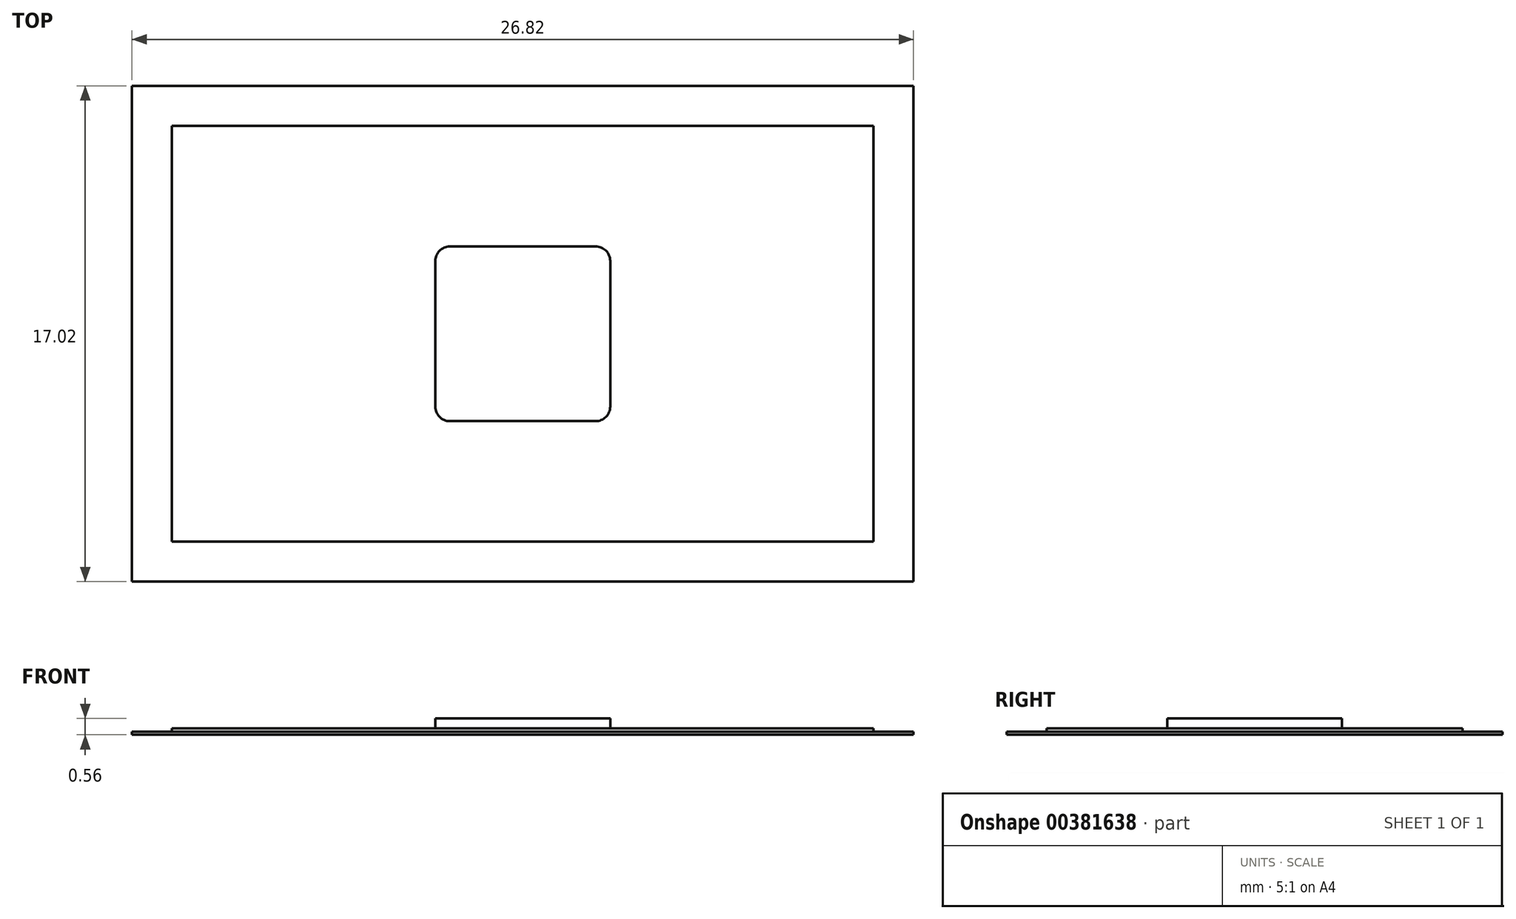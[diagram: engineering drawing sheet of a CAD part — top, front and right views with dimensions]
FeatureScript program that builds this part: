
annotation { "Feature Type Name" : "Feature", "Feature Type Description" : "" }
export const myFeature = defineFeature(function(context is Context, id is Id, definition is map)
    precondition{}
    {
        {
            var Q0;
            Q0=qCreatedBy(makeId("Top.planeOp"),FACE);
            var sketch = newSketch(context, id + "F0", { "sketchPlane" : qUnion([Q0])});
            skLineSegment(sketch, "E0.bottom", {"start": v(-12.29, 6.19) * mm, "end": v(14.53, 6.19) * mm});
            skLineSegment(sketch, "E0.top", {"start": v(-12.29, -10.83) * mm, "end": v(14.53, -10.83) * mm});
            skLineSegment(sketch, "E0.left", {"start": v(-12.29, 6.19) * mm, "end": v(-12.29, -10.83) * mm});
            skLineSegment(sketch, "E0.right", {"start": v(14.53, 6.19) * mm, "end": v(14.53, -10.83) * mm});
            skSolve(sketch);
        }
        {
            var Q0;
            Q0=makeQuery(id+"F0.imprint","IMPRINT",FACE,{"disambiguationData":[TD([[makeQuery(id+"F0.imprint","IMPRINT",EDGE,{"derivedFrom":sQuery(id+"F0.wireOp",EDGE,"E0.bottom")}),-1.0]])]});
            extrude(context, id + "F1", {"entities" : qUnion([Q0]), "depth" : 0.1 * mm});
        }
        {
            var Q0;
            Q0=makeQuery(id+"F1.opExtrude","CAP_FACE",FACE,{"disambiguationData":[OSD([sQuery(id+"F0.wireOp",EDGE,"E0.bottom"),sQuery(id+"F0.wireOp",EDGE,"E0.top"),sQuery(id+"F0.wireOp",EDGE,"E0.left"),sQuery(id+"F0.wireOp",EDGE,"E0.right")])],"isStart":false});
            var sketch = newSketch(context, id + "F2", { "sketchPlane" : qUnion([Q0])});
            skLineSegment(sketch, "E1.bottom", {"start": v(-10.92, 4.82) * mm, "end": v(13.16, 4.82) * mm});
            skLineSegment(sketch, "E1.top", {"start": v(-10.92, -9.46) * mm, "end": v(13.16, -9.46) * mm});
            skLineSegment(sketch, "E1.left", {"start": v(-10.92, 4.82) * mm, "end": v(-10.92, -9.46) * mm});
            skLineSegment(sketch, "E1.right", {"start": v(13.16, 4.82) * mm, "end": v(13.16, -9.46) * mm});
            skSolve(sketch);
        }
        {
            var Q0;
            Q0=makeQuery(id+"F2.imprint","IMPRINT",FACE,{"disambiguationData":[TD([[makeQuery(id+"F2.imprint","IMPRINT",EDGE,{"derivedFrom":sQuery(id+"F2.wireOp",EDGE,"E1.bottom")}),-1.0]])]});
            extrude(context, id + "F3", {"entities" : qUnion([Q0]), "operationType" : NewBodyOperationType.ADD, "depth" : 0.1 * mm});
        }
        {
            var Q0;
            Q0=makeQuery(id+"F3.opExtrude","CAP_FACE",FACE,{"disambiguationData":[OSD([sQuery(id+"F2.wireOp",EDGE,"E1.bottom"),sQuery(id+"F2.wireOp",EDGE,"E1.top"),sQuery(id+"F2.wireOp",EDGE,"E1.left"),sQuery(id+"F2.wireOp",EDGE,"E1.right")])],"isStart":false});
            var sketch = newSketch(context, id + "F4", { "sketchPlane" : qUnion([Q0])});
            skLineSegment(sketch, "E2.bottom", {"start": v(-1.38, 0.68) * mm, "end": v(3.62, 0.68) * mm});
            skLineSegment(sketch, "E2.top", {"start": v(-1.38, -5.32) * mm, "end": v(3.62, -5.32) * mm});
            skLineSegment(sketch, "E2.left", {"start": v(-1.88, 0.18) * mm, "end": v(-1.88, -4.82) * mm});
            skLineSegment(sketch, "E2.right", {"start": v(4.12, 0.18) * mm, "end": v(4.12, -4.82) * mm});
            skPoint(sketch, "E3.visualSharp", {"position": v(-1.88, 0.68) * mm});
            skArc(sketch, "E3.filletArc", {"start": v(-1.38, 0.68) * mm, "mid": v(-1.73, 0.53) * mm, "end": v(-1.88, 0.18) * mm});
            skPoint(sketch, "E4.visualSharp", {"position": v(-1.88, -5.32) * mm});
            skArc(sketch, "E4.filletArc", {"start": v(-1.88, -4.82) * mm, "mid": v(-1.73, -5.17) * mm, "end": v(-1.38, -5.32) * mm});
            skPoint(sketch, "E5.visualSharp", {"position": v(4.12, -5.32) * mm});
            skArc(sketch, "E5.filletArc", {"start": v(3.62, -5.32) * mm, "mid": v(3.97, -5.17) * mm, "end": v(4.12, -4.82) * mm});
            skPoint(sketch, "E6.visualSharp", {"position": v(4.12, 0.68) * mm});
            skArc(sketch, "E6.filletArc", {"start": v(4.12, 0.18) * mm, "mid": v(3.97, 0.53) * mm, "end": v(3.62, 0.68) * mm});
            skSolve(sketch);
        }
        {
            var Q0;
            Q0=makeQuery(id+"F4.imprint","IMPRINT",FACE,{"disambiguationData":[TD([[makeQuery(id+"F4.imprint","IMPRINT",EDGE,{"derivedFrom":sQuery(id+"F4.wireOp",EDGE,"E2.bottom")}),-1.0]])]});
            extrude(context, id + "F5", {"entities" : qUnion([Q0]), "operationType" : NewBodyOperationType.ADD, "depth" : 0.34 * mm});
        }
    });
